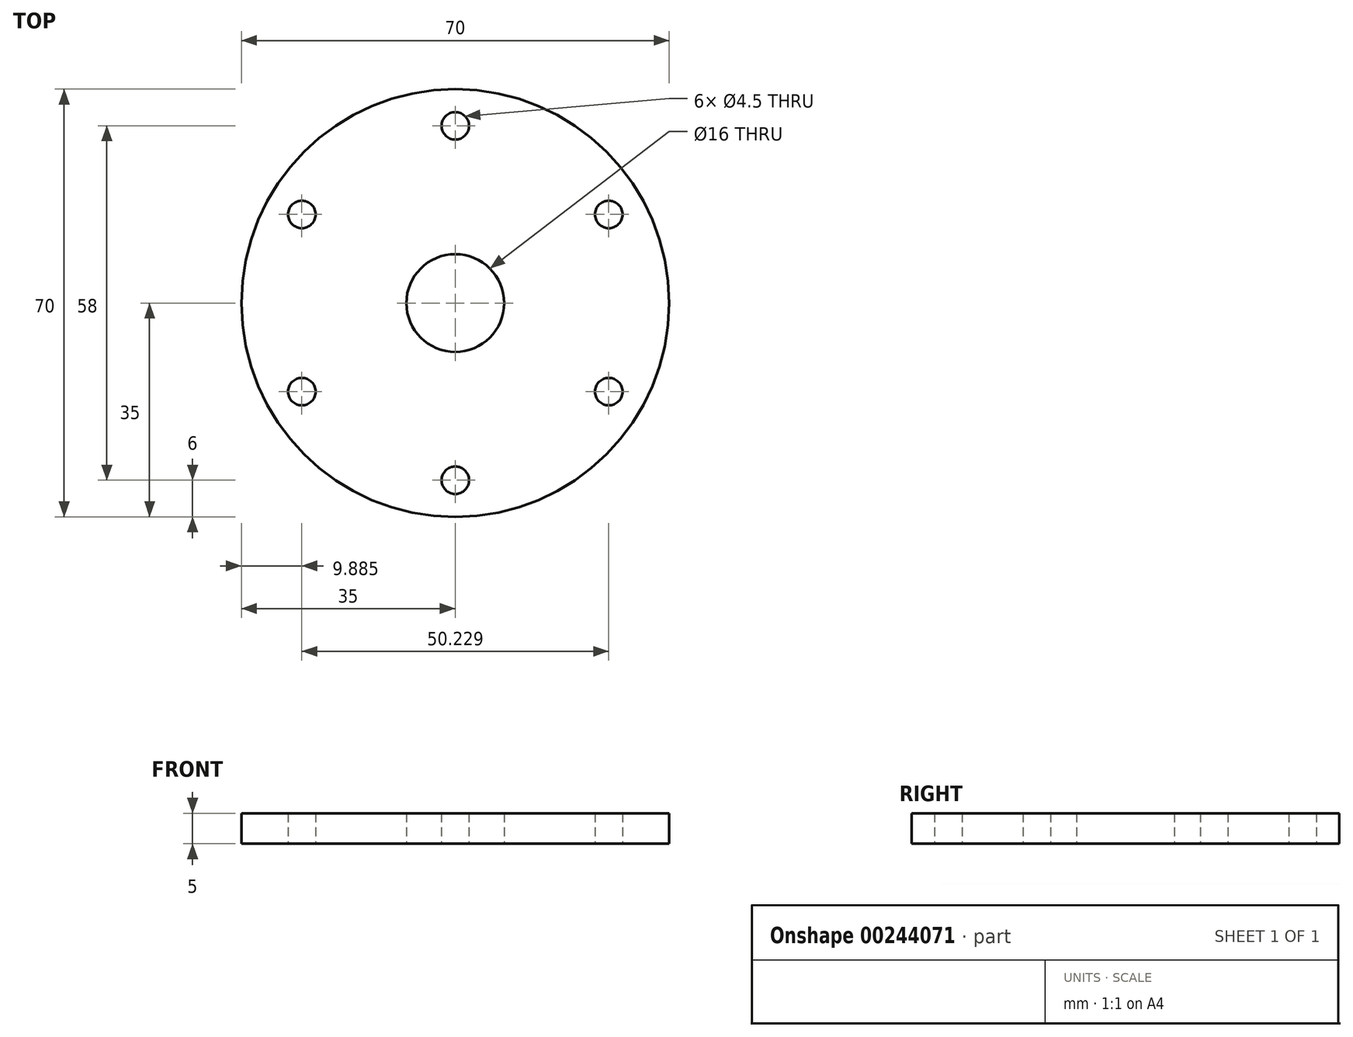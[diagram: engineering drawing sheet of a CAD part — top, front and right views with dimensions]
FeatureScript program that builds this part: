
annotation { "Feature Type Name" : "Feature", "Feature Type Description" : "" }
export const myFeature = defineFeature(function(context is Context, id is Id, definition is map)
    precondition{}
    {
        {
            var Q0;
            Q0=qCreatedBy(makeId("Top.planeOp"),FACE);
            var sketch = newSketch(context, id + "F0", { "sketchPlane" : qUnion([Q0])});
            skCircle(sketch, "E0", {"center": v(0, 0) * mm, "radius": 35 * mm});
            skCircle(sketch, "E1", {"center": v(0, 0) * mm, "radius": 8 * mm});
            skCircle(sketch, "E2", {"center": v(0, 29) * mm, "radius": 2.25 * mm});
            skCircle(sketch, "E3.1.0", {"center": v(-25.11, 14.5) * mm, "radius": 2.25 * mm});
            skCircle(sketch, "E3.2.0", {"center": v(-25.11, -14.5) * mm, "radius": 2.25 * mm});
            skCircle(sketch, "E3.3.0", {"center": v(0, -29) * mm, "radius": 2.25 * mm});
            skCircle(sketch, "E3.4.0", {"center": v(25.11, -14.5) * mm, "radius": 2.25 * mm});
            skCircle(sketch, "E3.5.0", {"center": v(25.11, 14.5) * mm, "radius": 2.25 * mm});
            skSolve(sketch);
        }
        {
            var Q0;
            Q0=makeQuery(id+"F0.imprint","IMPRINT",FACE,{"disambiguationData":[TD([[makeQuery(id+"F0.imprint","IMPRINT",EDGE,{"derivedFrom":sQuery(id+"F0.wireOp",EDGE,"E0")}),1.0]])]});
            extrude(context, id + "F1", {"entities" : qUnion([Q0]), "depth" : 5 * mm});
        }
    });
